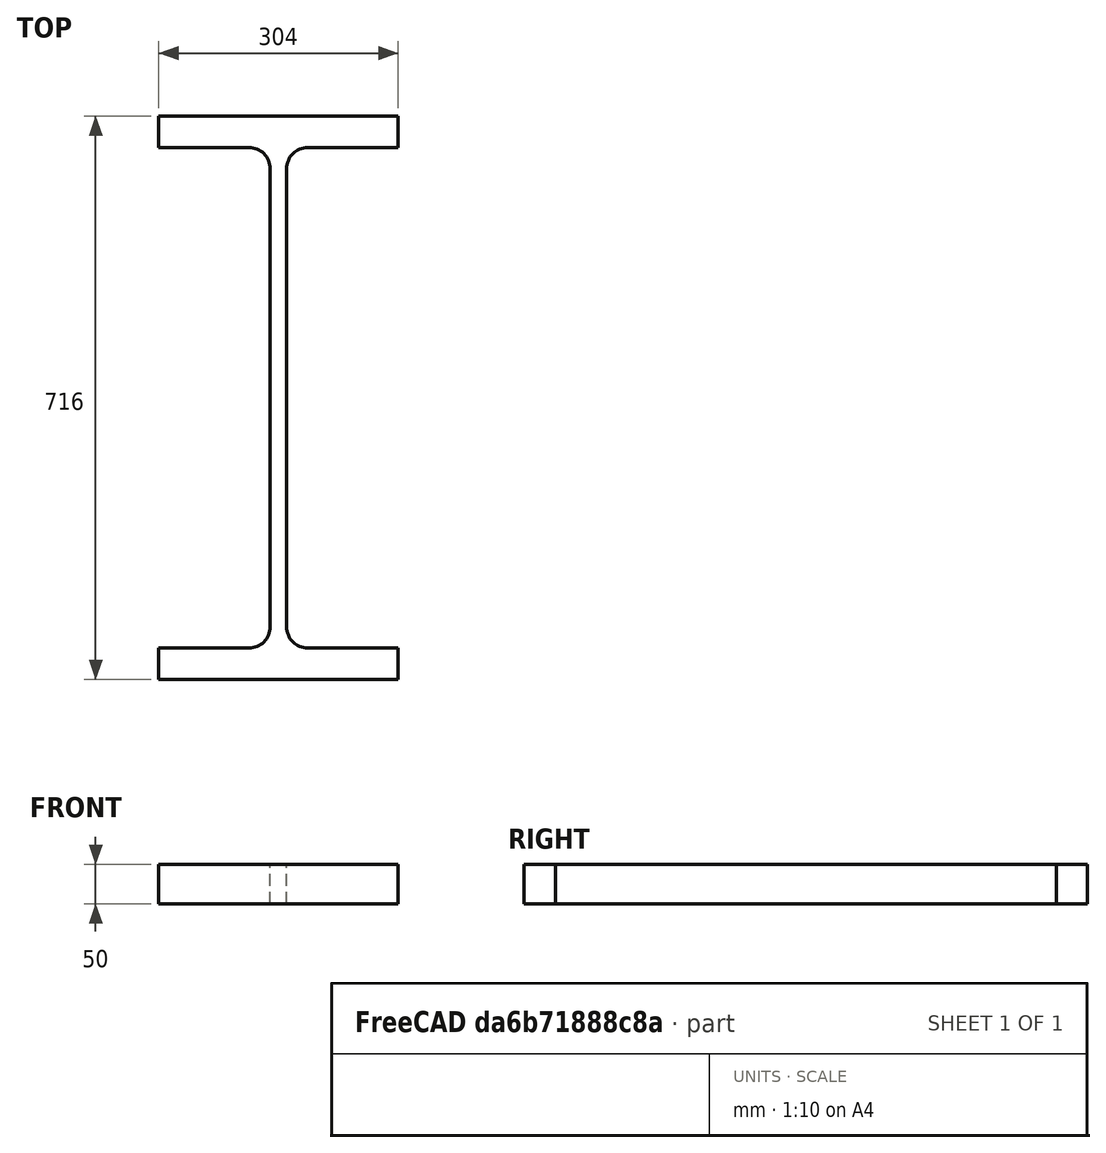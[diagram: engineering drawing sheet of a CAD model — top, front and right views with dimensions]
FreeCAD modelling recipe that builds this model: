
FCSTD DOCUMENT  (FreeCAD 0.15R4671 (Git))
Label: HE-M-Profile 700 DIN1025-4 S235JR
License: All rights reserved
LicenseURL: http://en.wikipedia.org/wiki/All_rights_reserved
objects: Sketcher::SketchObject×1, Part::Extrusion×1
note: 2 computed .brp shape members not serialized (recipe doc carries the construction recipe); baked Part::Feature solids carry a one-line shape summary decoded from their .brp

FEATURE [Sketcher::SketchObject] Sketch
  sketch-geometry (16):
    g0: LineSegment StartX=10.5 StartY=-291 StartZ=0 EndX=10.5 EndY=291 EndZ=0
    g1: LineSegment StartX=37.5 StartY=318 StartZ=0 EndX=152 EndY=318 EndZ=0
    g2: LineSegment StartX=152 StartY=318 StartZ=0 EndX=152 EndY=358 EndZ=0
    g3: LineSegment StartX=152 StartY=358 StartZ=0 EndX=-152 EndY=358 EndZ=0
    g4: LineSegment StartX=-152 StartY=358 StartZ=0 EndX=-152 EndY=318 EndZ=0
    g5: LineSegment StartX=-152 StartY=318 StartZ=0 EndX=-37.5 EndY=318 EndZ=0
    g6: LineSegment StartX=-10.5 StartY=291 StartZ=0 EndX=-10.5 EndY=-291 EndZ=0
    g7: LineSegment StartX=-37.5 StartY=-318 StartZ=0 EndX=-152 EndY=-318 EndZ=0
    g8: LineSegment StartX=-152 StartY=-318 StartZ=0 EndX=-152 EndY=-358 EndZ=0
    g9: LineSegment StartX=-152 StartY=-358 StartZ=0 EndX=152 EndY=-358 EndZ=0
    g10: LineSegment StartX=152 StartY=-358 StartZ=0 EndX=152 EndY=-318 EndZ=0
    g11: LineSegment StartX=152 StartY=-318 StartZ=0 EndX=37.5 EndY=-318 EndZ=0
    g12: ArcOfCircle CenterX=37.5 CenterY=291 CenterZ=0 NormalX=0 NormalY=0 NormalZ=1 Radius=27 StartAngle=1.5708 EndAngle=3.14159
    g13: ArcOfCircle CenterX=37.5 CenterY=-291 CenterZ=0 NormalX=0 NormalY=0 NormalZ=1 Radius=27 StartAngle=3.14159 EndAngle=4.71239
    g14: ArcOfCircle CenterX=-37.5 CenterY=291 CenterZ=0 NormalX=0 NormalY=0 NormalZ=1 Radius=27 StartAngle=0 EndAngle=1.5708
    g15: ArcOfCircle CenterX=-37.5 CenterY=-291 CenterZ=0 NormalX=0 NormalY=0 NormalZ=1 Radius=27 StartAngle=4.71239 EndAngle=6.28319
  constraints (42):
    c: Vertical(g0)
    c: Coincident(g2,g1)
    c: Vertical(g2)
    c: Coincident(g3,g2)
    c: Coincident(g4,g3)
    c: Vertical(g4)
    c: Coincident(g5,g4)
    c: Horizontal(g5)
    c: Vertical(g6)
    c: Horizontal(g7)
    c: Coincident(g8,g7)
    c: Vertical(g8)
    c: Coincident(g9,g8)
    c: Horizontal(g9)
    c: Coincident(g10,g9)
    c: Vertical(g10)
    c: Coincident(g11,g10)
    c: Horizontal(g11)
    c: Tangent(g1,g12) = 1.5708
    c: Tangent(g0,g12) = 1.5708
    c: Tangent(g0,g13) = 1.5708
    c: Tangent(g11,g13) = 1.5708
    c: Tangent(g5,g14) = 1.5708
    c: Tangent(g6,g14) = 1.5708
    c: Tangent(g6,g15) = 1.5708
    c: Tangent(g7,g15) = 1.5708
    c: Equal(g3,g9)
    c: Equal(g2,g4)
    c: Equal(g4,g8)
    c: Equal(g8,g10)
    c: Equal(g12,g14)
    c: Equal(g14,g15)
    c: Equal(g15,g13)
    c: Symmetric(g2,g3,g-2)
    c: Symmetric(g9,g8,g-2)
    c: Symmetric(g0,g6,g-2)
    c: Symmetric(g2,g9,g-1)
    c: DistanceY(g2,g9) = -716
    c: DistanceX(g3) = -304
    c: DistanceX(g0,g6) = -21
    c: DistanceY(g2) = 40
    c: Radius(g12) = 27
FEATURE [Part::Extrusion] Extrude  label="HE-M-Profile 700 DIN1025-4 S235JR"
  Base = -> Sketch
  Dir = (0,0,50)
  Solid = true
